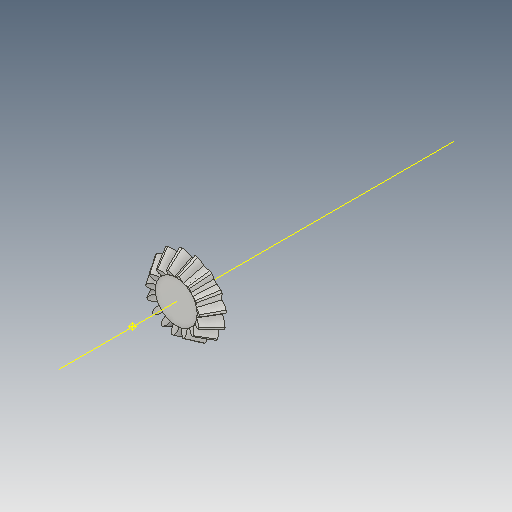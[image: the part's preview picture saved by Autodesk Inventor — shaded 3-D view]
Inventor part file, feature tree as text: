
AUTODESK INVENTOR PART (.ipt)
format: ipt  version: 2021 (Build 250183000, 183)  size: 482,816 bytes
history: native  units: mm
features: other x16, sketch x9, loft x3, pattern_circular x3
ambient origin geometry x6: Origin, XZ Plane, X Axis, Y Axis, Z Axis, Center Point
bodies: Solid1 (feature_tree)
feature tree (31):
  other  "Ponto superior"
  other  "Plano de malha 2"
  other  "Corpo dentado"
  other  "Ponto inicial"
  other  "Plano de dente"
  sketch  "Esboço inicial"  dims[d2=5.85633mm]
  other  "Extremidade"
  loft  "Loft"
  pattern_circular  "Circular Pattern"  [2 undecoded]
  sketch  "Esboço 3D direito"  dims[d3=1.5mm]
  other  "Plano final direito"
  loft  "Transição direita"
  pattern_circular  "Padrão circular direito"  [2 undecoded]
  sketch  "Esboço 3D esquerdo"  dims[d4=4.375097mm]
  other  "Plano final esquerdo"
  loft  "Transição esquerda"
  pattern_circular  "Padrão circular esquerdo"  Count=15 Angle=90.0deg
  other  "Fixar corpo"
  other  "Plano de malha"
  other  "Plano superior"
  sketch  "Esboço de corpo dentado"  dims[d5=90.0deg]
  other  "Plano final"
  sketch  "Esboço final"  dims[d7=1.153544mm]
  other  "Helical Curve Left"
  sketch  "Esboço final esquerdo"  dims[d8=1.311635mm]
  sketch  "Esboço de corpo"  dims[d9=2.506577mm]
  sketch  "Sketch6"  dims[d0=5.25mm d1=4.522404mm]
  other  "Srf1"
  other  "Helical Curve Right"
  sketch  "Esboço final direita"  dims[d11=1.5385mm d12=0.815688mm d15=0.927477mm d16=1.772438mm d17=0.0mm d18=90.0deg d19=0.0mm d20=90.0deg d21=150.0mm d22=360.0deg d26=33.647101mm d27=1.332627mm d28=5.25mm d29=-5.232783mm d30=0.815688mm d31=0.927477mm d32=1.772438mm d35=0.0mm d37=0.0mm d39=0.0mm d40=90.0deg d41=150.0mm d42=360.0deg d46=90.0deg d47=90.0deg d48=0.0mm d49=0.0mm d50=90.0deg d51=2.094395mm d52=0.0mm d53=0.0mm d54=0.0mm d56=1.812003mm d57=3.611528mm d58=2.518128mm d59=2.553766mm d60=1.780606mm d61=2.553766mm d62=1.780606mm d65=33.647101mm d66=31.5mm d67=5.25mm d68=-5.232783mm d69=1.332627mm d70=0.927477mm d71=1.772438mm d72=0.815688mm d73=1.780606mm d74=2.553766mm d75=0.0mm d77=0.0mm d79=0.0mm d80=90.0deg d81=150.0mm d82=360.0deg d84=10.0mm d85=20.0mm d86=20.0mm d87=10.0mm d88=0.0mm d89=0.0mm d90=90.0deg d91=90.0deg d92=90.0deg d93=90.0deg]
  other  "Diâmetro do flanco"
note: 4 required parameter values undecoded (feature->parameter linkage not recoverable at this tier; creation-order binding heuristic only, values carry confidence <= 0.55)
